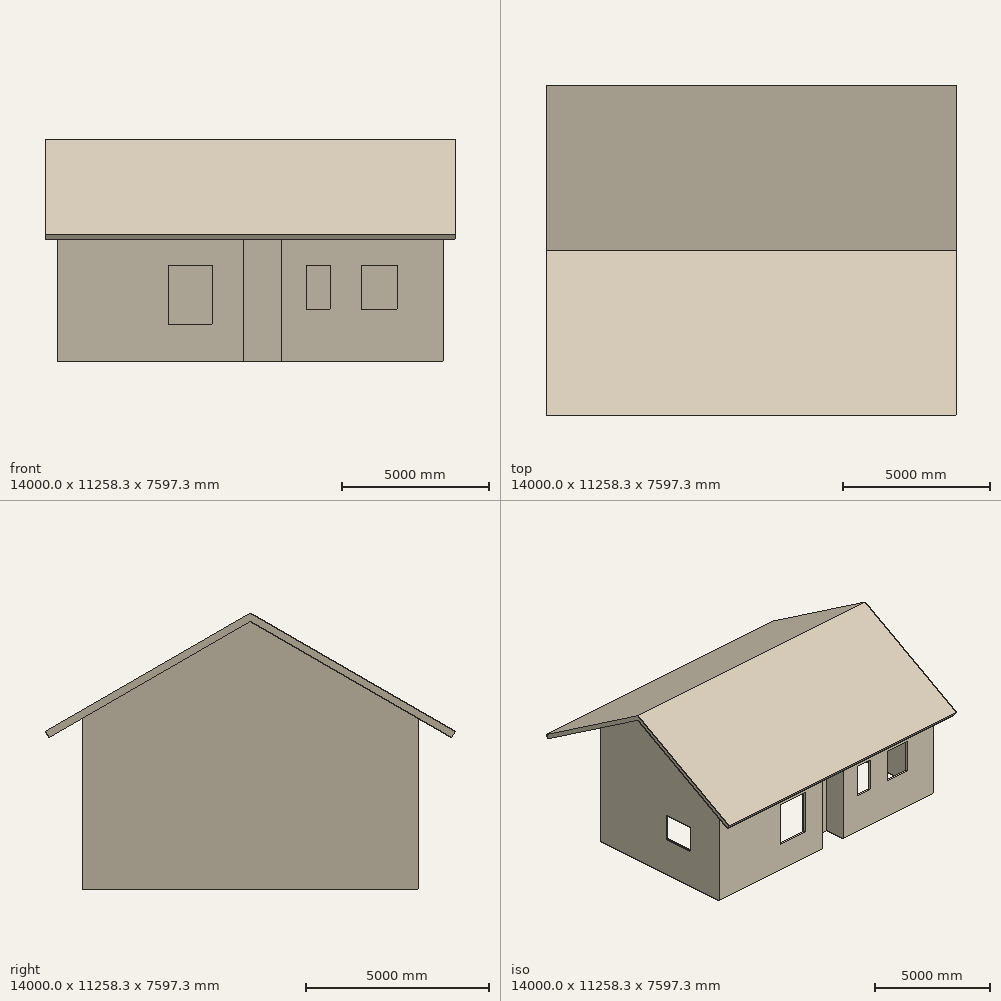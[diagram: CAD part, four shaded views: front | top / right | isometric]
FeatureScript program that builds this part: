
annotation { "Feature Type Name" : "Feature", "Feature Type Description" : "" }
export const myFeature = defineFeature(function(context is Context, id is Id, definition is map)
    precondition{}
    {
        {
            var Q0;
            Q0=qCreatedBy(makeId("Top.planeOp"),FACE);
            var sketch = newSketch(context, id + "F0", { "sketchPlane" : qUnion([Q0])});
            skLineSegment(sketch, "E0.bottom", {"start": v(100, 4500) * mm, "end": v(6500, 4500) * mm});
            skLineSegment(sketch, "E0.top", {"start": v(-6500, -4500) * mm, "end": v(-353.43, -4500) * mm});
            skLineSegment(sketch, "E0.left", {"start": v(-6500, 2609.87) * mm, "end": v(-6500, -4500) * mm});
            skLineSegment(sketch, "E0.right", {"start": v(6500, 4500) * mm, "end": v(6500, -4500) * mm});
            skPoint(sketch, "E0.middle", {"position": v(0, 0) * mm});
            skLineSegment(sketch, "E1", {"start": v(-353.43, -4500) * mm, "end": v(-353.43, -3500) * mm});
            skLineSegment(sketch, "E2", {"start": v(-353.43, -3500) * mm, "end": v(1146.57, -3500) * mm});
            skLineSegment(sketch, "E3", {"start": v(1146.57, -3500) * mm, "end": v(1146.57, -4500) * mm});
            skLineSegment(sketch, "E4.trimOffspring", {"start": v(1146.57, -4500) * mm, "end": v(6500, -4500) * mm});
            skLineSegment(sketch, "E5.0", {"start": v(-253.43, -3600) * mm, "end": v(1046.57, -3600) * mm});
            skLineSegment(sketch, "E5.1", {"start": v(-253.43, -4600) * mm, "end": v(-253.43, -3600) * mm});
            skLineSegment(sketch, "E5.2", {"start": v(1046.57, -3600) * mm, "end": v(1046.57, -4600) * mm});
            skLineSegment(sketch, "E5.3", {"start": v(-6600, -4600) * mm, "end": v(-253.43, -4600) * mm});
            skLineSegment(sketch, "E5.4", {"start": v(1046.57, -4600) * mm, "end": v(6600, -4600) * mm});
            skLineSegment(sketch, "E5.5", {"start": v(6600, 4600) * mm, "end": v(6600, -4600) * mm});
            skLineSegment(sketch, "E5.6", {"start": v(0, 4600) * mm, "end": v(6600, 4600) * mm});
            skLineSegment(sketch, "E5.7", {"start": v(-6600, 2609.87) * mm, "end": v(-6600, -4600) * mm});
            skLineSegment(sketch, "E6", {"start": v(0, 2709.87) * mm, "end": v(0, 4600) * mm});
            skLineSegment(sketch, "E7.0", {"start": v(100, 2609.87) * mm, "end": v(100, 4500) * mm});
            skLineSegment(sketch, "E8", {"start": v(100, 2609.87) * mm, "end": v(-6500, 2609.87) * mm});
            skLineSegment(sketch, "E9", {"start": v(0, 2709.87) * mm, "end": v(-6600, 2709.87) * mm});
            skLineSegment(sketch, "E10", {"start": v(-6600, 2709.87) * mm, "end": v(-6600, 2609.87) * mm});
            skSolve(sketch);
        }
        {
            var Q0;
            Q0=qCreatedBy(makeId("Right.planeOp"),FACE);
            var sketch = newSketch(context, id + "F1", { "sketchPlane" : qUnion([Q0])});
            skLineSegment(sketch, "E11", {"start": v(0, 7366.37) * mm, "end": v(-5529.17, 4174.1) * mm});
            skLineSegment(sketch, "E12", {"start": v(0, 7366.37) * mm, "end": v(5529.17, 4174.1) * mm});
            skLineSegment(sketch, "E13", {"start": v(-8602, 0) * mm, "end": v(-8602, 2400) * mm});
            skLineSegment(sketch, "E14.0", {"start": v(0, 7597.3) * mm, "end": v(5629.17, 4347.3) * mm});
            skLineSegment(sketch, "E14.1", {"start": v(0, 7597.3) * mm, "end": v(-5629.17, 4347.3) * mm});
            skLineSegment(sketch, "E15", {"start": v(-5629.17, 4347.3) * mm, "end": v(-5529.17, 4174.1) * mm});
            skLineSegment(sketch, "E16", {"start": v(5629.17, 4347.3) * mm, "end": v(5529.17, 4174.1) * mm});
            skSolve(sketch);
        }
        {
            var Q0;
            Q0=makeQuery(id+"F1.imprint","IMPRINT",FACE,{"disambiguationData":[TD([[makeQuery(id+"F1.imprint","IMPRINT",EDGE,{"derivedFrom":sQuery(id+"F1.wireOp",EDGE,"E11")}),-1.0]])]});
            var Q1;
            Q1=sQuery(id+"F1.wireOp",EDGE,"E12");
            var Q2;
            Q2=sQuery(id+"F1.wireOp",EDGE,"E11");
            extrude(context, id + "F2", {"entities" : qUnion([Q0]), "surfaceEntities" : qUnion([Q1, Q2]), "endBound" : BoundingType.SYMMETRIC, "depth" : 14000 * mm});
        }
        {
            var Q0;
            Q0 = qSketchRegion(id + "F0", true);
            var Q1;
            Q1=makeQuery(id+"F2.opExtrude","SWEPT_FACE",FACE,{"disambiguationData":[OSD([sQuery(id+"F1.wireOp",EDGE,"E11")])]});
            var Q2;
            Q2=makeQuery(id+"F2.opExtrude","SWEPT_BODY",BODY,{"disambiguationData":[OSD([sQuery(id+"F1.wireOp",EDGE,"E11")])]});
            extrude(context, id + "F3", {"entities" : qUnion([Q0]), "endBound" : BoundingType.UP_TO_BODY, "endBoundEntityFace" : qUnion([Q1]), "endBoundEntityBody" : qUnion([Q2]), "depth" : 25 * mm});
        }
        {
            var Q0;
            Q0=makeQuery(id+"F3.opExtrude","SWEPT_FACE",FACE,{"disambiguationData":[OSD([sQuery(id+"F0.wireOp",EDGE,"E5.3")])]});
            var sketch = newSketch(context, id + "F4", { "sketchPlane" : qUnion([Q0])});
            skLineSegment(sketch, "E17.bottom", {"start": v(-2801.16, 3281.5) * mm, "end": v(-1301.16, 3281.5) * mm});
            skLineSegment(sketch, "E17.top", {"start": v(-2801.16, 1281.5) * mm, "end": v(-1301.16, 1281.5) * mm});
            skLineSegment(sketch, "E17.left", {"start": v(-2801.16, 3281.5) * mm, "end": v(-2801.16, 1281.5) * mm});
            skLineSegment(sketch, "E17.right", {"start": v(-1301.16, 3281.5) * mm, "end": v(-1301.16, 1281.5) * mm});
            skLineSegment(sketch, "E18.bottom", {"start": v(1926.85, 3281.5) * mm, "end": v(2726.85, 3281.5) * mm});
            skLineSegment(sketch, "E18.top", {"start": v(1926.85, 1781.5) * mm, "end": v(2726.85, 1781.5) * mm});
            skLineSegment(sketch, "E18.left", {"start": v(1926.85, 3281.5) * mm, "end": v(1926.85, 1781.5) * mm});
            skLineSegment(sketch, "E18.right", {"start": v(2726.85, 3281.5) * mm, "end": v(2726.85, 1781.5) * mm});
            skLineSegment(sketch, "E19.bottom", {"start": v(3807.08, 3281.5) * mm, "end": v(5007.08, 3281.5) * mm});
            skLineSegment(sketch, "E19.top", {"start": v(3807.08, 1781.5) * mm, "end": v(5007.08, 1781.5) * mm});
            skLineSegment(sketch, "E19.left", {"start": v(3807.08, 3281.5) * mm, "end": v(3807.08, 1781.5) * mm});
            skLineSegment(sketch, "E19.right", {"start": v(5007.08, 3281.5) * mm, "end": v(5007.08, 1781.5) * mm});
            skSolve(sketch);
        }
        {
            var Q0;
            Q0 = qSketchRegion(id + "F4", true);
            var Q1;
            Q1=makeQuery(id+"F3.opExtrude","SWEPT_FACE",FACE,{"disambiguationData":[OSD([sQuery(id+"F0.wireOp",EDGE,"E0.top")])]});
            extrude(context, id + "F5", {"entities" : qUnion([Q0, Q1]), "operationType" : NewBodyOperationType.REMOVE, "endBound" : BoundingType.UP_TO_NEXT, "oppositeDirection" : true, "depth" : 25 * mm});
        }
        {
            var Q0;
            Q0=makeQuery(id+"F3.opExtrude","SWEPT_FACE",FACE,{"disambiguationData":[OSD([sQuery(id+"F0.wireOp",EDGE,"E5.7"),sQuery(id+"F0.wireOp",EDGE,"E10")])]});
            var sketch = newSketch(context, id + "F6", { "sketchPlane" : qUnion([Q0])});
            skLineSegment(sketch, "E20.bottom", {"start": v(1354.84, 2967.69) * mm, "end": v(2854.84, 2967.69) * mm});
            skLineSegment(sketch, "E20.top", {"start": v(1354.84, 1767.69) * mm, "end": v(2854.84, 1767.69) * mm});
            skLineSegment(sketch, "E20.left", {"start": v(1354.84, 2967.69) * mm, "end": v(1354.84, 1767.69) * mm});
            skLineSegment(sketch, "E20.right", {"start": v(2854.84, 2967.69) * mm, "end": v(2854.84, 1767.69) * mm});
            skSolve(sketch);
        }
        {
            var Q0;
            Q0 = qSketchRegion(id + "F6", true);
            var Q1;
            Q1=makeQuery(id+"F3.opExtrude","SWEPT_FACE",FACE,{"disambiguationData":[OSD([sQuery(id+"F0.wireOp",EDGE,"E0.left")])]});
            extrude(context, id + "F7", {"entities" : qUnion([Q0]), "operationType" : NewBodyOperationType.REMOVE, "endBound" : BoundingType.UP_TO_SURFACE, "oppositeDirection" : true, "endBoundEntityFace" : qUnion([Q1]), "depth" : 25 * mm});
        }
    });
